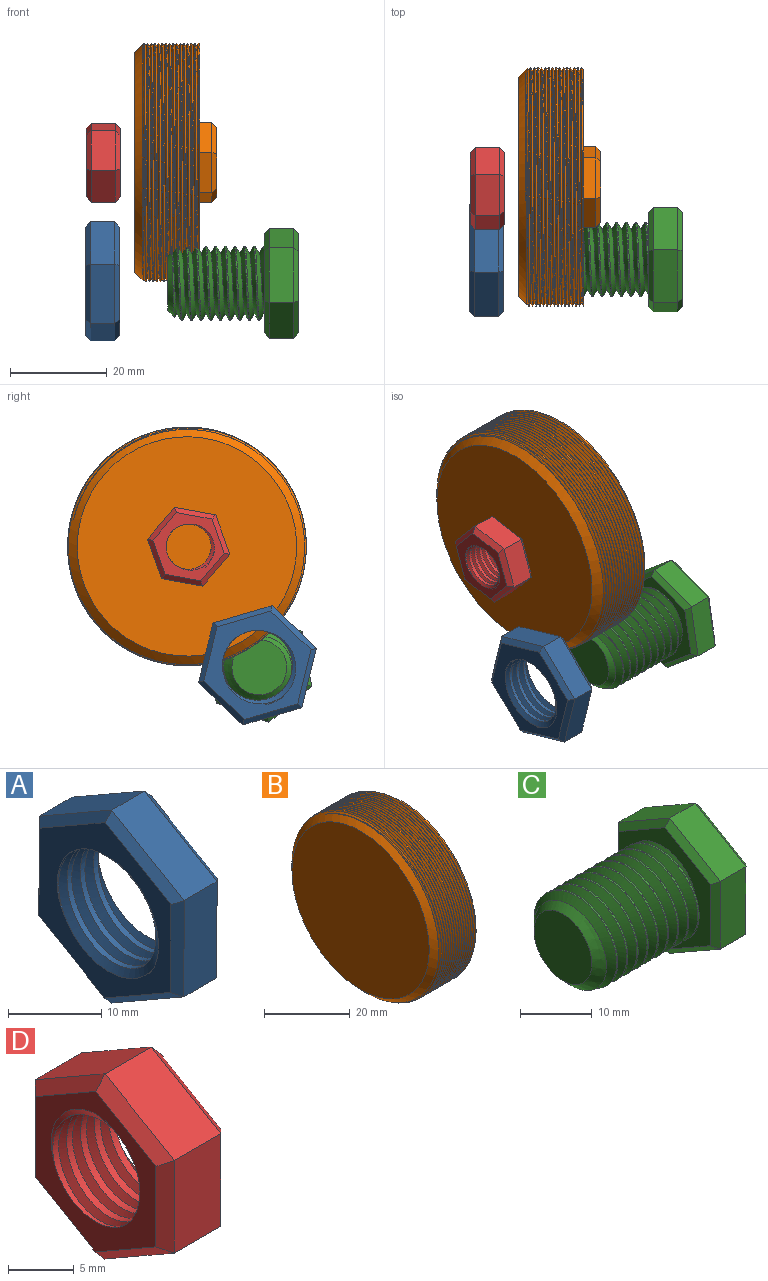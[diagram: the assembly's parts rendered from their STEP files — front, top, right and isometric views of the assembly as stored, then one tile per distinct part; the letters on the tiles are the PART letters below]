
ASSEMBLY  parts=4 mates=2
PART A: 23 faces, bbox 9.3x22.7x26 mm
  f0: cylinder r=7.24mm len=14.48mm, axis (1,0,0), area 111.6mm2, adj f7,f8,f21,f22
  f1: plane 10.98x6.38mm, normal (0,-0.5,0.86), area 63.5mm2, adj f2,f6,f14,f18
  f2: plane 12.7x5mm, normal (0,-1,0), area 63.5mm2, adj f1,f3,f12,f16
  f3: plane 11.02x6.32mm, normal (0,-0.5,-0.87), area 63.5mm2, adj f2,f4,f10,f15
  f4: plane 10.98x6.38mm, normal (0,0.5,-0.86), area 63.5mm2, adj f3,f5,f9,f17
  f5: plane 12.7x5mm, normal (0,1,0), area 63.5mm2, adj f4,f6,f11,f19
  f6: plane 11.02x6.32mm, normal (0,0.5,0.87), area 63.5mm2, adj f1,f5,f13,f20
  f7: plane 23.73x20.67mm, normal (-1,0,0), area 164.4mm2, adj f0,f9,f10,f11,f12,f13,f14,f21
  f8: plane 23.73x20.67mm, normal (1,0,0), area 164.4mm2, adj f0,f15,f16,f17,f18,f19,f20,f21
  f9: plane 10.99x6.96mm, normal (-0.71,0.36,-0.61), area 17.1mm2, adj f4,f7,f10,f11
  f10: plane 11.02x6.9mm, normal (-0.71,-0.35,-0.61), area 17.1mm2, adj f3,f7,f9,f12
  f11: plane 12.7x1.03mm, normal (-0.71,0.71,0), area 17.1mm2, adj f5,f7,f9,f13
  f12: plane 12.7x1.03mm, normal (-0.71,-0.71,0), area 17.1mm2, adj f2,f7,f10,f14
  f13: plane 11.02x6.9mm, normal (-0.71,0.35,0.61), area 17.1mm2, adj f6,f7,f11,f14
  f14: plane 10.99x6.96mm, normal (-0.71,-0.36,0.61), area 17.1mm2, adj f1,f7,f12,f13
  f15: plane 11.02x6.9mm, normal (0.71,-0.35,-0.61), area 17.1mm2, adj f3,f8,f16,f17
  f16: plane 12.7x1.03mm, normal (0.71,-0.71,0), area 17.1mm2, adj f2,f8,f15,f18
  f17: plane 10.99x6.96mm, normal (0.71,0.36,-0.61), area 17.1mm2, adj f4,f8,f15,f19
  f18: plane 10.99x6.96mm, normal (0.71,-0.36,0.61), area 17.1mm2, adj f1,f8,f16,f20
  f19: plane 12.7x1.03mm, normal (0.71,0.71,0), area 17.1mm2, adj f5,f8,f17,f20
  f20: plane 11.02x6.9mm, normal (0.71,0.35,0.61), area 17.1mm2, adj f6,f8,f18,f19
  f21: bspline ~19.31x16.73mm, area 223mm2, adj f0,f7,f8,f22
  f22: bspline ~19.31x16.73mm, area 223mm2, adj f0,f7,f8,f21
PART B: 20 faces, bbox 17.7x57.7x50.1 mm
  f0: cylinder r=24.7mm len=49.4mm, axis (1,0,0), area 211.8mm2, adj f2,f3,f4,f5,f6
  f1: plane 45.4x45.4mm, normal (-1,0,0), area 1618.8mm2, adj f3
  f2: plane 50.09x49.84mm, normal (1,0,0), area 1702.6mm2, adj f0,f4,f5,f7,f8,f9,f10,f11
  f3: cone r=24.7mm half-angle=45deg, axis (1,0,0), area 367.1mm2, adj f0,f1,f5,f6
  f4: plane 0.57x0.33mm, normal (0,1,0), area 0.1mm2, adj f0,f2,f6
  f5: bspline ~57.04x49.4mm, area 1581.1mm2, adj f0,f2,f3,f6
  f6: bspline ~57.04x49.4mm, area 1558.8mm2, adj f0,f3,f4,f5
  f7: plane 7.48x4.36mm, normal (0,-0.5,0.86), area 21.7mm2, adj f2,f8,f12,f19
  f8: plane 8.66x2.5mm, normal (0,-1,0), area 21.7mm2, adj f2,f7,f9,f17
  f9: plane 7.52x4.3mm, normal (0,-0.5,-0.87), area 21.7mm2, adj f2,f8,f10,f15
  f10: plane 7.48x4.36mm, normal (0,0.5,-0.86), area 21.7mm2, adj f2,f9,f11,f14
  f11: plane 8.66x2.5mm, normal (0,1,0), area 21.7mm2, adj f2,f10,f12,f16
  f12: plane 7.52x4.3mm, normal (0,0.5,0.87), area 21.7mm2, adj f2,f7,f11,f18
  f13: plane 15.01x13.03mm, normal (1,0,0), area 146.4mm2, adj f14,f15,f16,f17,f18,f19
  f14: plane 7.49x4.93mm, normal (0.71,0.36,-0.61), area 11.4mm2, adj f10,f13,f15,f16
  f15: plane 7.52x4.88mm, normal (0.71,-0.35,-0.61), area 11.4mm2, adj f9,f13,f14,f17
  f16: plane 8.66x1.03mm, normal (0.71,0.71,0), area 11.4mm2, adj f11,f13,f14,f18
  f17: plane 8.66x1.03mm, normal (0.71,-0.71,0), area 11.4mm2, adj f8,f13,f15,f19
  f18: plane 7.52x4.88mm, normal (0.71,0.35,0.61), area 11.4mm2, adj f12,f13,f16,f19
  f19: plane 7.49x4.93mm, normal (0.71,-0.36,0.61), area 11.4mm2, adj f7,f13,f17,f18
PART C: 26 faces, bbox 27.7x20x23.1 mm
  f0: cylinder r=7.68mm len=18mm, axis (1,0,0), area 139.1mm2, adj f1,f2,f5,f13
  f1: bspline ~20.88x17.74mm, area 713.8mm2, adj f0,f2,f4,f5,f13
  f2: bspline ~21.88x17.74mm, area 715.1mm2, adj f0,f1,f4,f5,f13
  f3: plane 11.36x11.36mm, normal (-1,0,0), area 101.4mm2, adj f4
  f4: cone r=7.68mm half-angle=45deg, axis (1,0,0), area 63.2mm2, adj f1,f2,f3,f5
  f5: cone r=7.68mm half-angle=45deg, axis (1,0,0), area 13.2mm2, adj f0,f1,f2,f4
  f6: plane 9.98x5.81mm, normal (0,-0.5,0.86), area 57.7mm2, adj f7,f11,f19,f23
  f7: plane 11.55x5mm, normal (0,-1,0), area 57.7mm2, adj f6,f8,f17,f21
  f8: plane 10.02x5.74mm, normal (0,-0.5,-0.87), area 57.7mm2, adj f7,f9,f15,f20
  f9: plane 9.98x5.81mm, normal (0,0.5,-0.86), area 57.7mm2, adj f8,f10,f14,f22
  f10: plane 11.55x5mm, normal (0,1,0), area 57.7mm2, adj f9,f11,f16,f24
  f11: plane 10.02x5.74mm, normal (0,0.5,0.87), area 57.7mm2, adj f6,f10,f18,f25
  f12: plane 20.78x18.04mm, normal (1,0,0), area 280.6mm2, adj f14,f15,f16,f17,f18,f19
  f13: plane 20.78x18.04mm, normal (-1,0,0), area 125.2mm2, adj f0,f1,f2,f20,f21,f22,f23,f24
  f14: plane 9.98x6.38mm, normal (0.71,0.36,-0.61), area 15.5mm2, adj f9,f12,f15,f16
  f15: plane 10.02x6.32mm, normal (0.71,-0.35,-0.61), area 15.5mm2, adj f8,f12,f14,f17
  f16: plane 11.55x1.04mm, normal (0.71,0.71,0), area 15.5mm2, adj f10,f12,f14,f18
  f17: plane 11.55x1.04mm, normal (0.71,-0.71,0), area 15.5mm2, adj f7,f12,f15,f19
  f18: plane 10.02x6.32mm, normal (0.71,0.35,0.61), area 15.5mm2, adj f11,f12,f16,f19
  f19: plane 9.98x6.38mm, normal (0.71,-0.36,0.61), area 15.5mm2, adj f6,f12,f17,f18
  f20: plane 10.02x6.32mm, normal (-0.71,-0.35,-0.61), area 15.5mm2, adj f8,f13,f21,f22
  f21: plane 11.55x1.04mm, normal (-0.71,-0.71,0), area 15.5mm2, adj f7,f13,f20,f23
  f22: plane 9.98x6.38mm, normal (-0.71,0.36,-0.61), area 15.5mm2, adj f9,f13,f20,f24
  f23: plane 9.98x6.38mm, normal (-0.71,-0.36,0.61), area 15.5mm2, adj f6,f13,f21,f25
  f24: plane 11.55x1.04mm, normal (-0.71,0.71,0), area 15.5mm2, adj f10,f13,f22,f25
  f25: plane 10.02x6.32mm, normal (-0.71,0.35,0.61), area 15.5mm2, adj f11,f13,f23,f24
PART D: 23 faces, bbox 9.1x15.4x17.7 mm
  f0: plane 7.49x5mm, normal (0,-0.5,0.86), area 43.3mm2, adj f1,f5,f13,f17
  f1: plane 8.66x5mm, normal (0,-1,0), area 43.3mm2, adj f0,f2,f11,f15
  f2: plane 7.51x5mm, normal (0,-0.5,-0.87), area 43.3mm2, adj f1,f3,f9,f14
  f3: plane 7.49x5mm, normal (0,0.5,-0.86), area 43.3mm2, adj f2,f4,f8,f16
  f4: plane 8.66x5mm, normal (0,1,0), area 43.3mm2, adj f3,f5,f10,f18
  f5: plane 7.51x5mm, normal (0,0.5,0.87), area 43.3mm2, adj f0,f4,f12,f19
  f6: plane 15.37x13.38mm, normal (-1,0,0), area 71.4mm2, adj f8,f9,f10,f11,f12,f13,f20,f21
  f7: plane 15.37x13.38mm, normal (1,0,0), area 71.4mm2, adj f14,f15,f16,f17,f18,f19,f20,f21
  f8: plane 7.49x4.93mm, normal (-0.71,0.36,-0.61), area 11.4mm2, adj f3,f6,f9,f10
  f9: plane 7.51x4.89mm, normal (-0.71,-0.35,-0.61), area 11.4mm2, adj f2,f6,f8,f11
  f10: plane 8.66x1.02mm, normal (-0.71,0.71,0), area 11.4mm2, adj f4,f6,f8,f12
  f11: plane 8.66x1.02mm, normal (-0.71,-0.71,0), area 11.4mm2, adj f1,f6,f9,f13
  f12: plane 7.51x4.89mm, normal (-0.71,0.35,0.61), area 11.4mm2, adj f5,f6,f10,f13
  f13: plane 7.49x4.93mm, normal (-0.71,-0.36,0.61), area 11.4mm2, adj f0,f6,f11,f12
  f14: plane 7.51x4.89mm, normal (0.71,-0.35,-0.61), area 11.4mm2, adj f2,f7,f15,f16
  f15: plane 8.66x1.02mm, normal (0.71,-0.71,0), area 11.4mm2, adj f1,f7,f14,f17
  f16: plane 7.49x4.93mm, normal (0.71,0.36,-0.61), area 11.4mm2, adj f3,f7,f14,f18
  f17: plane 7.49x4.93mm, normal (0.71,-0.36,0.61), area 11.4mm2, adj f0,f7,f15,f19
  f18: plane 8.66x1.02mm, normal (0.71,0.71,0), area 11.4mm2, adj f4,f7,f16,f19
  f19: plane 7.51x4.89mm, normal (0.71,0.35,0.61), area 11.4mm2, adj f5,f7,f17,f18
  f20: cylinder r=4.66mm len=9.32mm, axis (1,0,0), area 85.4mm2, adj f6,f7,f21,f22
  f21: bspline ~12.5x10.82mm, area 128.4mm2, adj f6,f7,f20,f22
  f22: bspline ~12.5x10.82mm, area 128.5mm2, adj f6,f7,f20,f21
PLACE A rot(axis=(0,0.6,-0.8),180deg) t=(-55.27,-6.86,23.48)mm fixed
PLACE B rot(axis=(-1,0,0),43.8deg) t=(-31.66,7.73,48.08)mm
PLACE C rot(axis=(1,0,0),109.9deg) t=(-14.77,-7.25,23.06)mm
PLACE D rot(axis=(1,0,0),100.2deg) t=(-48.16,7.38,48.02)mm fixed
MATE cylindrical C.f0 <-> A.f7  axis (-1,0,0) through (-38.27,-7.25,23.06)mm
MATE cylindrical B.f0 <-> D.f6  axis (-1,0,0) through (-45.16,7.73,48.08)mm
